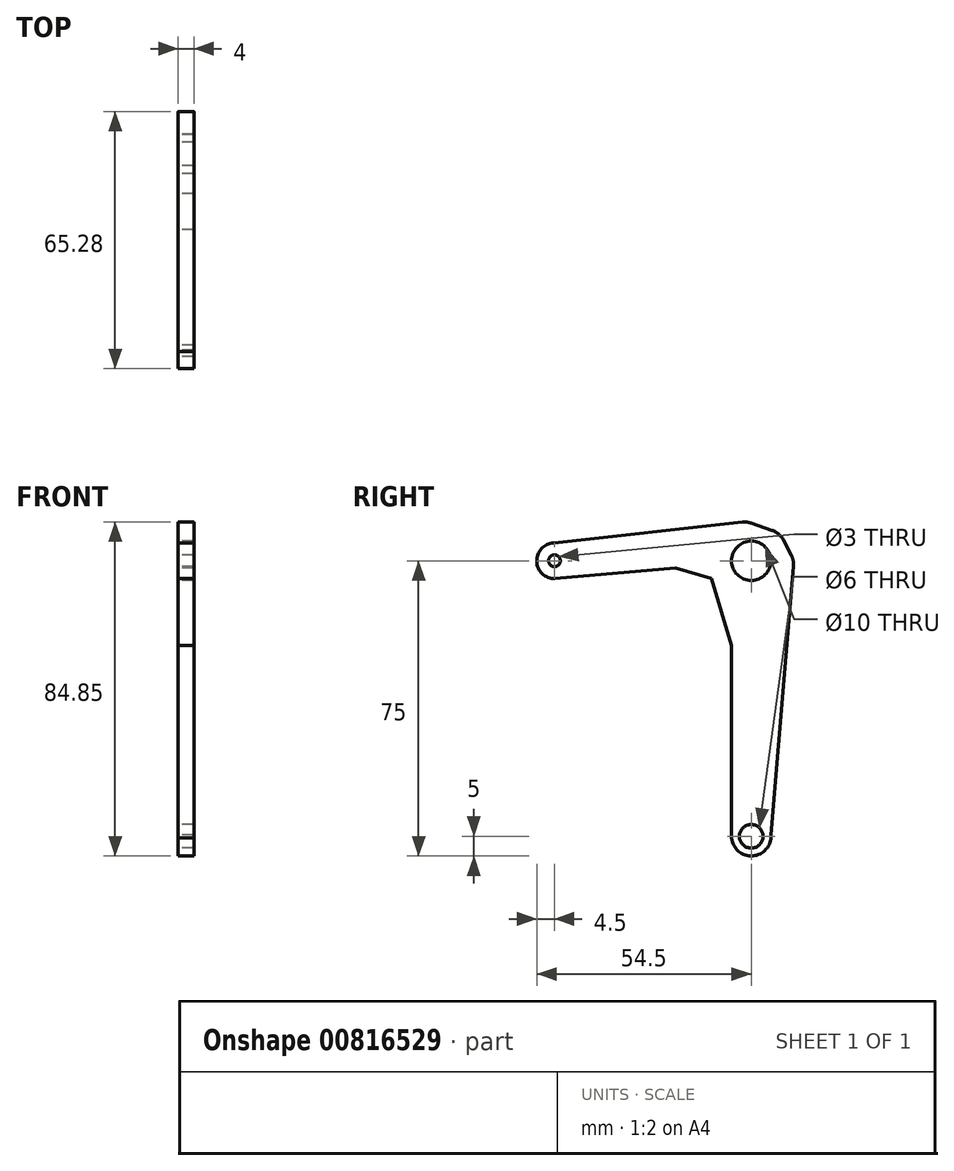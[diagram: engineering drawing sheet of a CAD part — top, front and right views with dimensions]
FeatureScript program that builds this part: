
annotation { "Feature Type Name" : "Feature", "Feature Type Description" : "" }
export const myFeature = defineFeature(function(context is Context, id is Id, definition is map)
    precondition{}
    {
        {
            var Q0;
            Q0=qCreatedBy(makeId("Right.planeOp"),FACE);
            var sketch = newSketch(context, id + "F0", { "sketchPlane" : qUnion([Q0])});
            skCircle(sketch, "E0", {"center": v(0, 0) * mm, "radius": 5 * mm});
            skCircle(sketch, "E1", {"center": v(-50, 0) * mm, "radius": 1.5 * mm});
            skCircle(sketch, "E2", {"center": v(0, -70) * mm, "radius": 3 * mm});
            skArc(sketch, "E3", {"start": v(-50.17, 4.5) * mm, "mid": v(-54.5, -0.16) * mm, "end": v(-49.85, -4.5) * mm});
            skArc(sketch, "E4", {"start": v(-4.98, -70.41) * mm, "mid": v(0.38, -74.99) * mm, "end": v(4.99, -69.65) * mm});
            skLineSegment(sketch, "E5", {"start": v(-50.17, 4.5) * mm, "end": v(-2.21, 9.82) * mm});
            skLineSegment(sketch, "E6", {"start": v(4.86, -71.18) * mm, "end": v(10.76, -1.44) * mm});
            skLineSegment(sketch, "E7", {"start": v(-4.98, -70.41) * mm, "end": v(-4.98, -21.57) * mm});
            skLineSegment(sketch, "E8", {"start": v(-49.85, -4.5) * mm, "end": v(-19.23, -1.78) * mm});
            skLineSegment(sketch, "E9", {"start": v(-19.23, -1.78) * mm, "end": v(-10.07, -4.5) * mm});
            skLineSegment(sketch, "E10", {"start": v(-10.07, -4.5) * mm, "end": v(-4.98, -21.57) * mm});
            skLineSegment(sketch, "E11", {"start": v(-0.04, 9.58) * mm, "end": v(5.3, 7.75) * mm});
            skLineSegment(sketch, "E12", {"start": v(8.12, 5.32) * mm, "end": v(10.21, 1.28) * mm});
            skPoint(sketch, "E13.visualSharp", {"position": v(-1.1, 9.94) * mm});
            skArc(sketch, "E13.filletArc", {"start": v(-0.04, 9.58) * mm, "mid": v(-1.12, 9.82) * mm, "end": v(-2.21, 9.82) * mm});
            skPoint(sketch, "E14.visualSharp", {"position": v(7.2, 7.1) * mm});
            skArc(sketch, "E14.filletArc", {"start": v(8.12, 5.32) * mm, "mid": v(6.94, 6.8) * mm, "end": v(5.3, 7.75) * mm});
            skPoint(sketch, "E15.visualSharp", {"position": v(10.88, 0) * mm});
            skArc(sketch, "E15.filletArc", {"start": v(10.76, -1.44) * mm, "mid": v(10.68, -0.04) * mm, "end": v(10.21, 1.28) * mm});
            skSolve(sketch);
        }
        {
            var Q0;
            Q0 = qSketchRegion(id + "F0", true);
            extrude(context, id + "F1", {"entities" : qUnion([Q0]), "depth" : 4 * mm, "offsetDistance" : 25 * mm});
        }
    });
